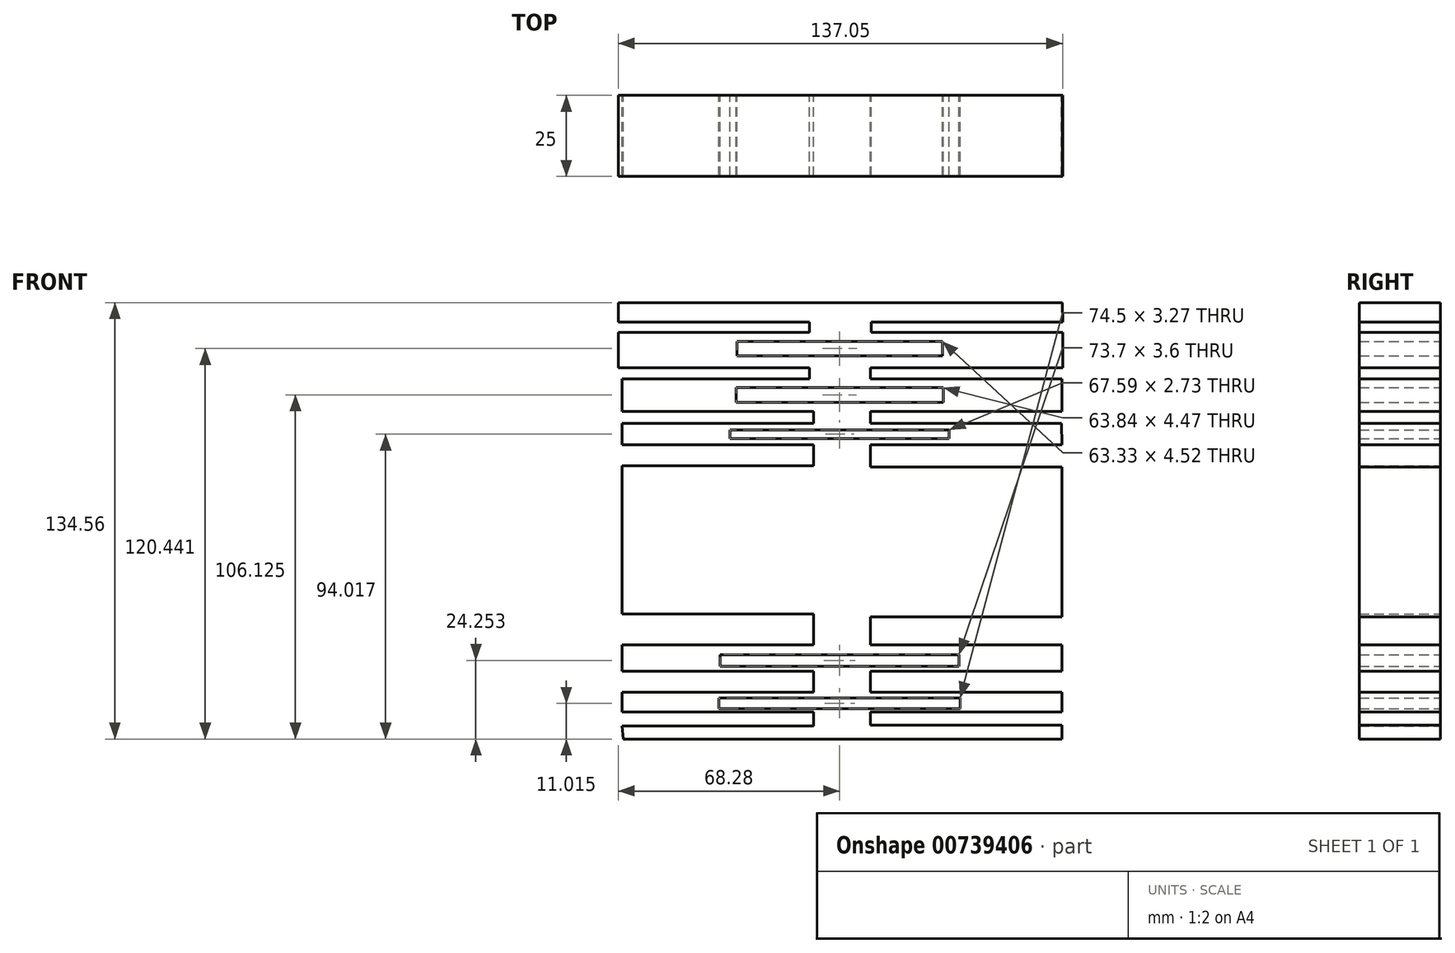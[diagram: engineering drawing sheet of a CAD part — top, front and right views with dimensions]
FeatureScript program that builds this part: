
annotation { "Feature Type Name" : "Feature", "Feature Type Description" : "" }
export const myFeature = defineFeature(function(context is Context, id is Id, definition is map)
    precondition{}
    {
        {
            var Q0;
            Q0=qCreatedBy(makeId("Front.planeOp"),FACE);
            var sketch = newSketch(context, id + "F0", { "sketchPlane" : qUnion([Q0])});
            skLineSegment(sketch, "E0", {"start": v(-68.28, 66.55) * mm, "end": v(-68.28, 55.58) * mm});
            skLineSegment(sketch, "E1", {"start": v(68.77, 66.55) * mm, "end": v(68.77, 55.58) * mm});
            skLineSegment(sketch, "E2", {"start": v(68.77, 55.58) * mm, "end": v(9.54, 55.58) * mm});
            skLineSegment(sketch, "E3", {"start": v(-68.28, 55.58) * mm, "end": v(-9.27, 55.58) * mm});
            skLineSegment(sketch, "E4", {"start": v(-9.27, 55.58) * mm, "end": v(-9.27, 52.23) * mm});
            skLineSegment(sketch, "E5", {"start": v(9.54, 55.58) * mm, "end": v(9.54, 52.23) * mm});
            skLineSegment(sketch, "E6", {"start": v(9.54, 52.23) * mm, "end": v(68.55, 52.23) * mm});
            skLineSegment(sketch, "E7", {"start": v(-9.27, 52.23) * mm, "end": v(-67.06, 52.23) * mm});
            skLineSegment(sketch, "E8.bottom", {"start": v(31.67, 63.82) * mm, "end": v(-31.67, 63.82) * mm});
            skLineSegment(sketch, "E8.top", {"start": v(31.67, 59.3) * mm, "end": v(-31.67, 59.3) * mm});
            skLineSegment(sketch, "E8.left", {"start": v(31.67, 63.82) * mm, "end": v(31.67, 59.3) * mm});
            skLineSegment(sketch, "E8.right", {"start": v(-31.67, 63.82) * mm, "end": v(-31.67, 59.3) * mm});
            skPoint(sketch, "E8.middle", {"position": v(0, 61.56) * mm});
            skLineSegment(sketch, "E9", {"start": v(-67.06, 52.23) * mm, "end": v(-67.06, 42.15) * mm});
            skLineSegment(sketch, "E10", {"start": v(68.55, 52.23) * mm, "end": v(68.55, 42.15) * mm});
            skLineSegment(sketch, "E11", {"start": v(68.55, 42.15) * mm, "end": v(9.54, 42.15) * mm});
            skLineSegment(sketch, "E12", {"start": v(-67.06, 42.15) * mm, "end": v(-8.06, 42.15) * mm});
            skLineSegment(sketch, "E13", {"start": v(-8.06, 42.15) * mm, "end": v(-8.06, 38.48) * mm});
            skLineSegment(sketch, "E14", {"start": v(-8.06, 38.48) * mm, "end": v(-67.06, 38.48) * mm});
            skLineSegment(sketch, "E15", {"start": v(-67.06, 38.48) * mm, "end": v(-67.06, 31.92) * mm});
            skLineSegment(sketch, "E16.bottom", {"start": v(31.92, 49.48) * mm, "end": v(-31.92, 49.48) * mm});
            skLineSegment(sketch, "E16.top", {"start": v(31.92, 45.01) * mm, "end": v(-31.92, 45.01) * mm});
            skLineSegment(sketch, "E16.left", {"start": v(31.92, 49.48) * mm, "end": v(31.92, 45.01) * mm});
            skLineSegment(sketch, "E16.right", {"start": v(-31.92, 49.48) * mm, "end": v(-31.92, 45.01) * mm});
            skPoint(sketch, "E16.middle", {"position": v(0, 47.25) * mm});
            skPoint(sketch, "E17.start.orphan", {"position": v(0, 66.55) * mm});
            skLineSegment(sketch, "E18", {"start": v(-68.28, 66.55) * mm, "end": v(-9.27, 66.55) * mm});
            skLineSegment(sketch, "E19", {"start": v(68.77, 66.55) * mm, "end": v(9.76, 66.55) * mm});
            skLineSegment(sketch, "E20", {"start": v(-9.27, 66.55) * mm, "end": v(-9.27, 69.74) * mm});
            skLineSegment(sketch, "E21", {"start": v(-9.27, 69.74) * mm, "end": v(-68.28, 69.74) * mm});
            skLineSegment(sketch, "E22", {"start": v(-68.28, 69.74) * mm, "end": v(-68.28, 75.68) * mm});
            skLineSegment(sketch, "E23", {"start": v(-68.28, 75.68) * mm, "end": v(0, 75.68) * mm});
            skLineSegment(sketch, "E24", {"start": v(9.76, 66.55) * mm, "end": v(9.76, 69.74) * mm});
            skLineSegment(sketch, "E25", {"start": v(9.76, 69.74) * mm, "end": v(68.77, 69.74) * mm});
            skLineSegment(sketch, "E26", {"start": v(0, 75.68) * mm, "end": v(68.7, 75.68) * mm});
            skLineSegment(sketch, "E27", {"start": v(68.77, 69.74) * mm, "end": v(68.7, 75.68) * mm});
            skLineSegment(sketch, "E28", {"start": v(9.54, 42.15) * mm, "end": v(9.45, 38.48) * mm});
            skLineSegment(sketch, "E29", {"start": v(9.45, 38.48) * mm, "end": v(68.46, 38.48) * mm});
            skLineSegment(sketch, "E30", {"start": v(68.46, 38.48) * mm, "end": v(68.55, 31.92) * mm});
            skLineSegment(sketch, "E31", {"start": v(68.55, 31.92) * mm, "end": v(9.54, 31.92) * mm});
            skLineSegment(sketch, "E32", {"start": v(-67.06, 31.92) * mm, "end": v(-8.06, 31.92) * mm});
            skLineSegment(sketch, "E33", {"start": v(9.54, 31.92) * mm, "end": v(9.54, 25.04) * mm});
            skLineSegment(sketch, "E34.bottom", {"start": v(33.8, 36.5) * mm, "end": v(-33.8, 36.5) * mm});
            skLineSegment(sketch, "E34.top", {"start": v(33.8, 33.77) * mm, "end": v(-33.8, 33.77) * mm});
            skLineSegment(sketch, "E34.left", {"start": v(33.8, 36.5) * mm, "end": v(33.8, 33.77) * mm});
            skLineSegment(sketch, "E34.right", {"start": v(-33.8, 36.5) * mm, "end": v(-33.8, 33.77) * mm});
            skPoint(sketch, "E34.middle", {"position": v(0, 35.14) * mm});
            skLineSegment(sketch, "E35", {"start": v(-8.06, 31.92) * mm, "end": v(-8.06, 25.36) * mm});
            skLineSegment(sketch, "E36", {"start": v(9.54, 25.04) * mm, "end": v(68.55, 25.04) * mm});
            skLineSegment(sketch, "E37", {"start": v(-8.06, 25.36) * mm, "end": v(-67.06, 25.36) * mm});
            skLineSegment(sketch, "E38", {"start": v(68.55, 25.04) * mm, "end": v(68.55, -21.2) * mm});
            skLineSegment(sketch, "E39", {"start": v(-67.06, 25.36) * mm, "end": v(-67.06, -20.29) * mm});
            skLineSegment(sketch, "E40", {"start": v(-67.06, -20.29) * mm, "end": v(-8.06, -20.29) * mm});
            skLineSegment(sketch, "E41", {"start": v(68.55, -21.2) * mm, "end": v(9.54, -21.2) * mm});
            skLineSegment(sketch, "E42", {"start": v(9.54, -21.2) * mm, "end": v(9.54, -29.88) * mm});
            skLineSegment(sketch, "E43", {"start": v(-8.06, -20.29) * mm, "end": v(-8.06, -29.88) * mm});
            skLineSegment(sketch, "E44", {"start": v(9.54, -29.88) * mm, "end": v(68.55, -29.88) * mm});
            skLineSegment(sketch, "E45", {"start": v(-8.06, -29.88) * mm, "end": v(-67.06, -29.88) * mm});
            skLineSegment(sketch, "E46", {"start": v(68.55, -29.88) * mm, "end": v(68.55, -37.92) * mm});
            skLineSegment(sketch, "E47", {"start": v(68.55, -37.92) * mm, "end": v(9.54, -37.92) * mm});
            skLineSegment(sketch, "E48", {"start": v(-67.06, -29.88) * mm, "end": v(-67.06, -37.92) * mm});
            skLineSegment(sketch, "E49", {"start": v(-67.06, -37.92) * mm, "end": v(-8.06, -37.92) * mm});
            skLineSegment(sketch, "E50.bottom", {"start": v(36.85, -32.83) * mm, "end": v(-36.85, -32.83) * mm});
            skLineSegment(sketch, "E50.top", {"start": v(36.85, -36.43) * mm, "end": v(-36.85, -36.43) * mm});
            skLineSegment(sketch, "E50.left", {"start": v(36.85, -32.83) * mm, "end": v(36.85, -36.43) * mm});
            skLineSegment(sketch, "E50.right", {"start": v(-36.85, -32.83) * mm, "end": v(-36.85, -36.43) * mm});
            skPoint(sketch, "E50.middle", {"position": v(0, -34.63) * mm});
            skLineSegment(sketch, "E51", {"start": v(9.54, -37.92) * mm, "end": v(9.54, -44.45) * mm});
            skLineSegment(sketch, "E52", {"start": v(9.54, -44.45) * mm, "end": v(68.55, -44.45) * mm});
            skLineSegment(sketch, "E53", {"start": v(-8.06, -37.92) * mm, "end": v(-8.06, -44.45) * mm});
            skLineSegment(sketch, "E54", {"start": v(-8.06, -44.45) * mm, "end": v(-67.06, -44.45) * mm});
            skLineSegment(sketch, "E55", {"start": v(-67.06, -44.45) * mm, "end": v(-67.06, -50.51) * mm});
            skLineSegment(sketch, "E56", {"start": v(-67.06, -50.51) * mm, "end": v(-8.06, -50.51) * mm});
            skLineSegment(sketch, "E57", {"start": v(68.55, -44.45) * mm, "end": v(68.55, -50.51) * mm});
            skLineSegment(sketch, "E58", {"start": v(68.55, -50.51) * mm, "end": v(9.54, -50.51) * mm});
            skLineSegment(sketch, "E59.bottom", {"start": v(37.25, -46.23) * mm, "end": v(-37.25, -46.23) * mm});
            skLineSegment(sketch, "E59.top", {"start": v(37.25, -49.5) * mm, "end": v(-37.25, -49.5) * mm});
            skLineSegment(sketch, "E59.left", {"start": v(37.25, -46.23) * mm, "end": v(37.25, -49.5) * mm});
            skLineSegment(sketch, "E59.right", {"start": v(-37.25, -46.23) * mm, "end": v(-37.25, -49.5) * mm});
            skPoint(sketch, "E59.middle", {"position": v(0, -47.87) * mm});
            skLineSegment(sketch, "E60", {"start": v(9.54, -50.51) * mm, "end": v(9.54, -54.6) * mm});
            skLineSegment(sketch, "E61", {"start": v(9.54, -54.6) * mm, "end": v(68.55, -54.6) * mm});
            skLineSegment(sketch, "E62", {"start": v(68.55, -54.6) * mm, "end": v(68.55, -58.88) * mm});
            skLineSegment(sketch, "E63", {"start": v(68.55, -58.88) * mm, "end": v(0.27, -58.88) * mm});
            skLineSegment(sketch, "E64", {"start": v(-8.06, -50.51) * mm, "end": v(-8.06, -54.82) * mm});
            skLineSegment(sketch, "E65", {"start": v(-8.06, -54.82) * mm, "end": v(-67.06, -54.82) * mm});
            skLineSegment(sketch, "E66", {"start": v(0.27, -58.88) * mm, "end": v(-66.76, -58.88) * mm});
            skLineSegment(sketch, "E67", {"start": v(-67.06, -54.82) * mm, "end": v(-66.76, -58.88) * mm});
            skSolve(sketch);
        }
        {
            var Q0;
            Q0 = qSketchRegion(id + "F0", true);
            extrude(context, id + "F1", {"entities" : qUnion([Q0]), "depth" : 25 * mm, "offsetDistance" : 25 * mm});
        }
    });
